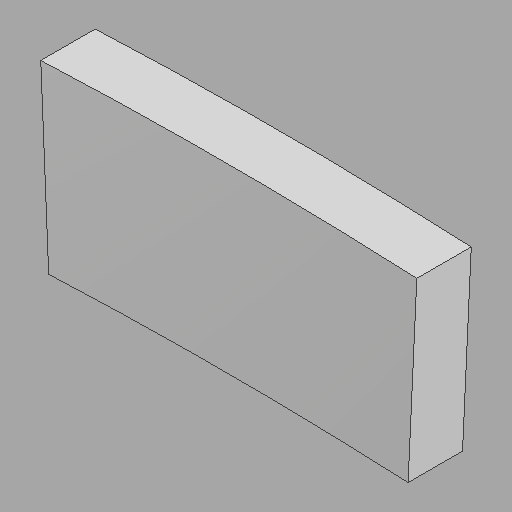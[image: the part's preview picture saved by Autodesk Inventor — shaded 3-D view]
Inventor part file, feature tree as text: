
AUTODESK INVENTOR PART (.ipt)
format: ipt  version: 2022.1 (Build 261234020, 234B)  size: 89,600 bytes
history: imported  units: in
note: dims shown in document units (in); Inventor stores cm internally (conversion verified against a paired STEP export)
features: imported_body x1
ambient origin geometry x8: Origin, YZ Plane, XZ Plane, XY Plane, X Axis, Y Axis, Z Axis, Center Point
bodies: Solid1 (imported_parasolid), Body1 (imported_parasolid)
feature tree (1):
  imported_body  NMx_Import_Brep_tag  [imported B-rep: ~6 faces, bbox_mm=[1053.068993, 509.28941, 152.4]]
